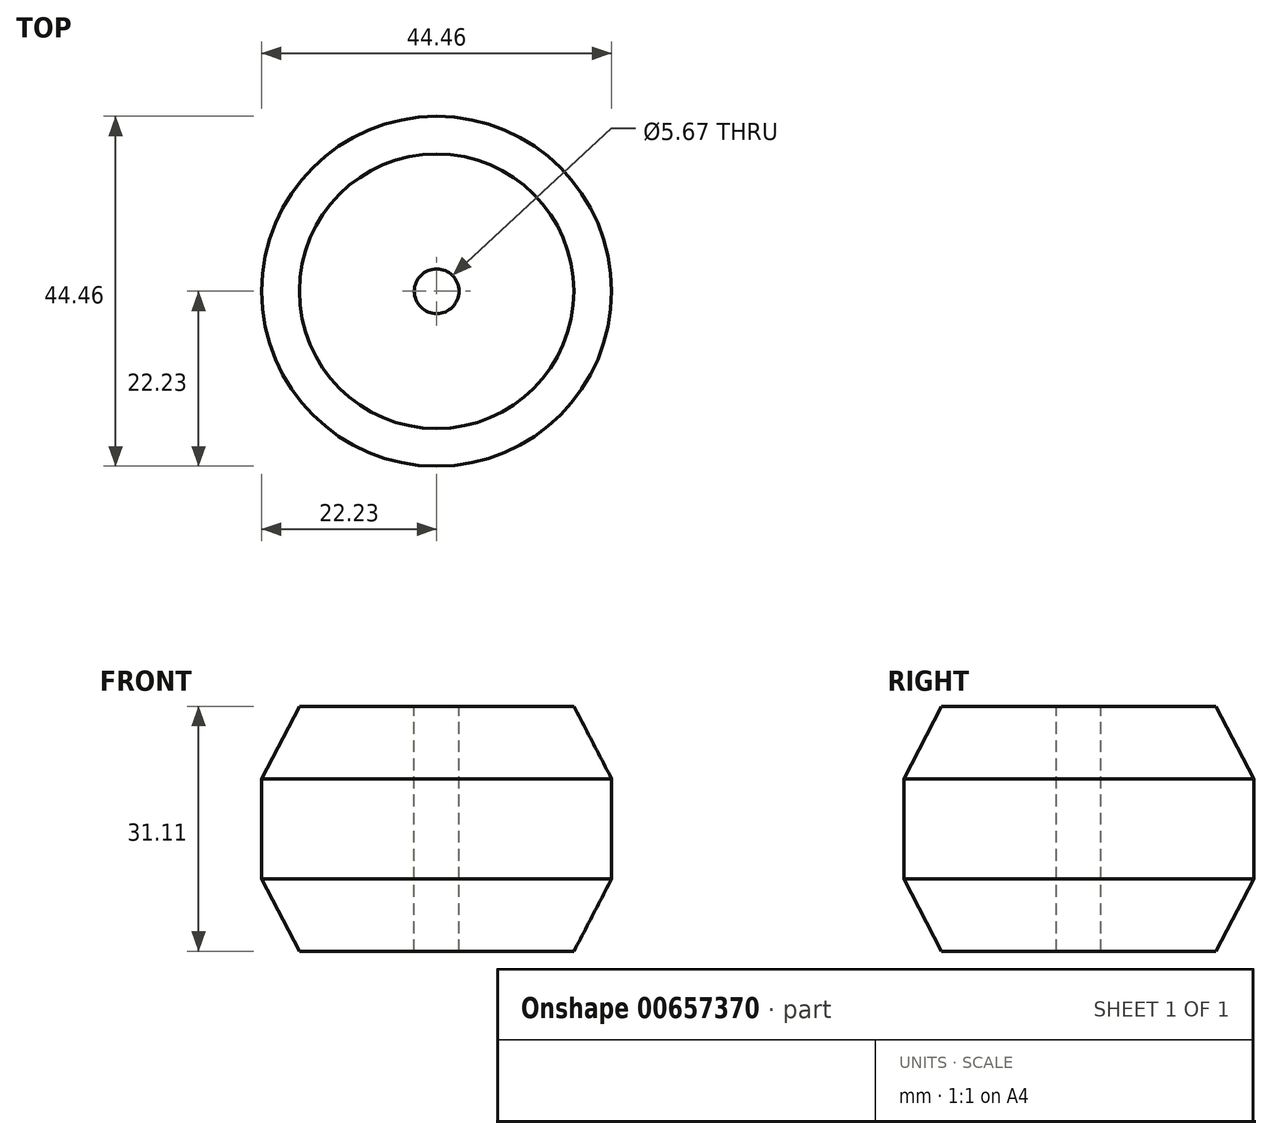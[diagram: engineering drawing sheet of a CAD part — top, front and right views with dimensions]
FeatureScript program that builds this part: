
annotation { "Feature Type Name" : "Feature", "Feature Type Description" : "" }
export const myFeature = defineFeature(function(context is Context, id is Id, definition is map)
    precondition{}
    {
        {
            var Q0;
            Q0=qCreatedBy(makeId("Front.planeOp"),FACE);
            var sketch = newSketch(context, id + "F0", { "sketchPlane" : qUnion([Q0])});
            skLineSegment(sketch, "E0", {"start": v(0, -19.8) * mm, "end": v(0, -54.73) * mm, "construction": true});
            skLineSegment(sketch, "E1", {"start": v(22.23, -29) * mm, "end": v(22.23, -41.7) * mm});
            skLineSegment(sketch, "E2", {"start": v(17.44, -50.91) * mm, "end": v(22.23, -41.7) * mm});
            skLineSegment(sketch, "E3", {"start": v(17.44, -19.8) * mm, "end": v(22.23, -29) * mm});
            skLineSegment(sketch, "E4", {"start": v(17.44, -19.8) * mm, "end": v(2.84, -19.8) * mm});
            skLineSegment(sketch, "E5", {"start": v(17.44, -50.91) * mm, "end": v(2.84, -50.91) * mm});
            skLineSegment(sketch, "E6", {"start": v(2.84, -19.8) * mm, "end": v(2.84, -50.91) * mm});
            skLineSegment(sketch, "E7", {"start": v(2.84, -35.36) * mm, "end": v(39.14, -35.36) * mm, "construction": true});
            skSolve(sketch);
        }
        {
            var Q0;
            Q0=makeQuery(id+"F0.imprint","IMPRINT",FACE,{"disambiguationData":[TD([[makeQuery(id+"F0.imprint","IMPRINT",EDGE,{"derivedFrom":sQuery(id+"F0.wireOp",EDGE,"E1")}),-1.0]])]});
            var Q1;
            Q1=sQuery(id+"F0.wireOp",EDGE,"E4");
            var Q2;
            Q2=sQuery(id+"F0.wireOp",EDGE,"E3");
            var Q3;
            Q3=sQuery(id+"F0.wireOp",EDGE,"E1");
            var Q4;
            Q4=sQuery(id+"F0.wireOp",EDGE,"E2");
            var Q5;
            Q5=sQuery(id+"F0.wireOp",EDGE,"E5");
            var Q6;
            Q6=sQuery(id+"F0.wireOp",EDGE,"E6");
            var Q7;
            Q7=sQuery(id+"F0.wireOp",EDGE,"E0");
            revolve(context, id + "F1", {"surfaceOperationType" : NewSurfaceOperationType.NEW, "entities" : qUnion([Q0]), "surfaceEntities" : qUnion([Q1, Q2, Q3, Q4, Q5, Q6]), "axis" : qUnion([Q7]), "revolveType" : RevolveType.FULL});
        }
    });
